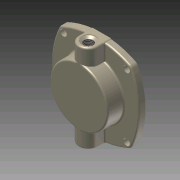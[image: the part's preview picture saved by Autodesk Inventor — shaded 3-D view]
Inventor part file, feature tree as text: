
AUTODESK INVENTOR PART (.ipt)
format: ipt  version: 2011 (Build 150239000, 239)  size: 407,552 bytes
history: native  units: in
note: dims shown in document units (in); Inventor stores cm internally (conversion verified against a paired STEP export)
features: extrude x8, sketch x8, plane x4, loft x2, thread x2, fillet x2, projected_geometry x1
ambient origin geometry x8: Origin, YZ Plane, XZ Plane, XY Plane, X Axis, Y Axis, Z Axis, Center Point
bodies: Solid1 (feature_tree)
feature tree (27):
  extrude  "Extrusion1"  Depth=0.25in
  extrude  "Extrusion2"  Depth=2.425in
  plane  "Work Plane1"
  sketch  "Sketch3"  dims[d7=0.25in d8=0.0in d9=2.225in]
  plane  "Work Plane2"
  extrude  "Extrusion3"  Depth=2.225in
  sketch  "Sketch4"  dims[d10=0.625in d11=0.0in d12=0.75in]
  plane  "Work Plane3"
  loft  "Loft1"
  extrude  "Extrusion5"  Depth=0.5in
  extrude  "Extrusion6"  Depth=2.125in
  sketch  "Sketch6"  dims[d15=0.625in d16=0.0in d19=2.125in]
  extrude  "Extrusion7"  Depth=2.0in
  extrude  "Extrusion8"  TaperAngle=0.0deg  [1 undecoded]
  plane  "Work Plane4"
  loft  "Loft2"
  thread  "Thread1"  [1 undecoded]
  thread  "Thread2"  [1 undecoded]
  fillet  "Fillet1"  Radius=0.05in
  extrude  "Extrusion9"  Depth=0.35in
  fillet  "Fillet2"  Radius=0.05in
  sketch  "Sketch1"  dims[d1=3.375in d2=0.25in]
  sketch  "Sketch2"  dims[d3=2.425in d4=2.425in]
  sketch  "Sketch5"  dims[d13=-3.375in d14=0.5in]
  sketch  "Sketch7"  dims[d20=-0.75in d21=2.0in]
  projected_geometry  "Projected Loop1"
  sketch  "Sketch8"  dims[d22=0.0in d23=90.0deg d24=0.0in d25=90.0deg d26=2.5in d27=2.625in d28=0.05in d29=0.0in d30=0.05in d31=0.0in d32=0.35in d33=0.05in d34=0.0in d35=0.55in d36=0.0125in d37=0.0in d38=-0.075in d39=0.0in d40=90.0deg d41=0.0in d42=90.0deg d43=0.39in d44=0.0in d45=1.0in d46=0.0in d48=0.0625in d49=0.625in d50=0.125in d51=0.0in d52=0.0375in d53=0.25in d54=2.425in d55=2.425in d56=3.375in d57=0.1in d58=0.1in d59=0.1in d60=0.1in d61=2.6693in d62=2.6693in]
note: 3 required parameter values undecoded (feature->parameter linkage not recoverable at this tier; creation-order binding heuristic only, values carry confidence <= 0.55)
